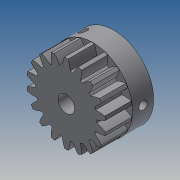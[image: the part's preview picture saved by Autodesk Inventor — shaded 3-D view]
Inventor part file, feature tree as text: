
AUTODESK INVENTOR PART (.ipt)
format: ipt  version: 2017 (Build 210142000, 142)  size: 293,376 bytes
history: native  units: mm
features: extrude x4, other x3, sketch x3, pattern_circular x1, chamfer x1, projected_geometry x1
ambient origin geometry x8: Origin, YZ Plane, XZ Plane, XY Plane, X Axis, Y Axis, Z Axis, Center Point
bodies: Body1 (feature_tree)
feature tree (13):
  other  "Sólido1"
  extrude  "Extrusión1"  Depth=12.0mm
  sketch  "Boceto2"  dims[d3=6.0mm d4=3.0mm]
  extrude  "Extrusión2"  Depth=3.0mm
  extrude  "Extrusión3"  Depth=10.0mm
  extrude  "Extrusión4"  TaperAngle=120.0deg  [1 undecoded]
  other  "Dientes de engranaje recto3"
  pattern_circular  "Patrón circular1"  [2 undecoded]
  chamfer  "Chaflán1"  Distance=16.0mm
  sketch  "Boceto1"  dims[d0=6.3mm d2=12.0mm]
  projected_geometry  "Contorno proyectado1"
  sketch  "Boceto3"  dims[d5=8.0mm d6=0.0mm d7=3.2mm d8=120.0deg d9=2.95mm d10=16.0mm d11=0.0mm d12=4.0mm d13=0.0mm d14=10.0mm d15=0.0mm d16=30.0mm d18=360.0deg d20=30.0mm d21=360.0deg d23=1.0mm d24=2.0mm d25=45.0deg]
  other  "iFeature1:3"
note: 3 required parameter values undecoded (feature->parameter linkage not recoverable at this tier; creation-order binding heuristic only, values carry confidence <= 0.55)
